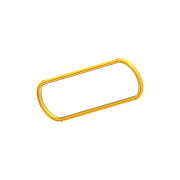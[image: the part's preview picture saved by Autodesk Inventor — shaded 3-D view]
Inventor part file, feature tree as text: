
AUTODESK INVENTOR PART (.ipt)
format: ipt  version: 2012 (Build 160160000, 160)  size: 96,256 bytes
history: native  units: in
note: dims shown in document units (in); Inventor stores cm internally (conversion verified against a paired STEP export)
features: extrude x1, fillet x1, sketch x1
ambient origin geometry x8: Origin, YZ Plane, XZ Plane, XY Plane, X Axis, Y Axis, Z Axis, Center Point
bodies: Solid1 (feature_tree)
feature tree (3):
  extrude  "Extrusion1"  Depth=0.95in
  fillet  "Fillet1"  Radius=0.1875in
  sketch  "Sketch1"  dims[d0=0.1875in d1=0.95in d2=0.1875in d3=0.0in d4=0.0938in]
